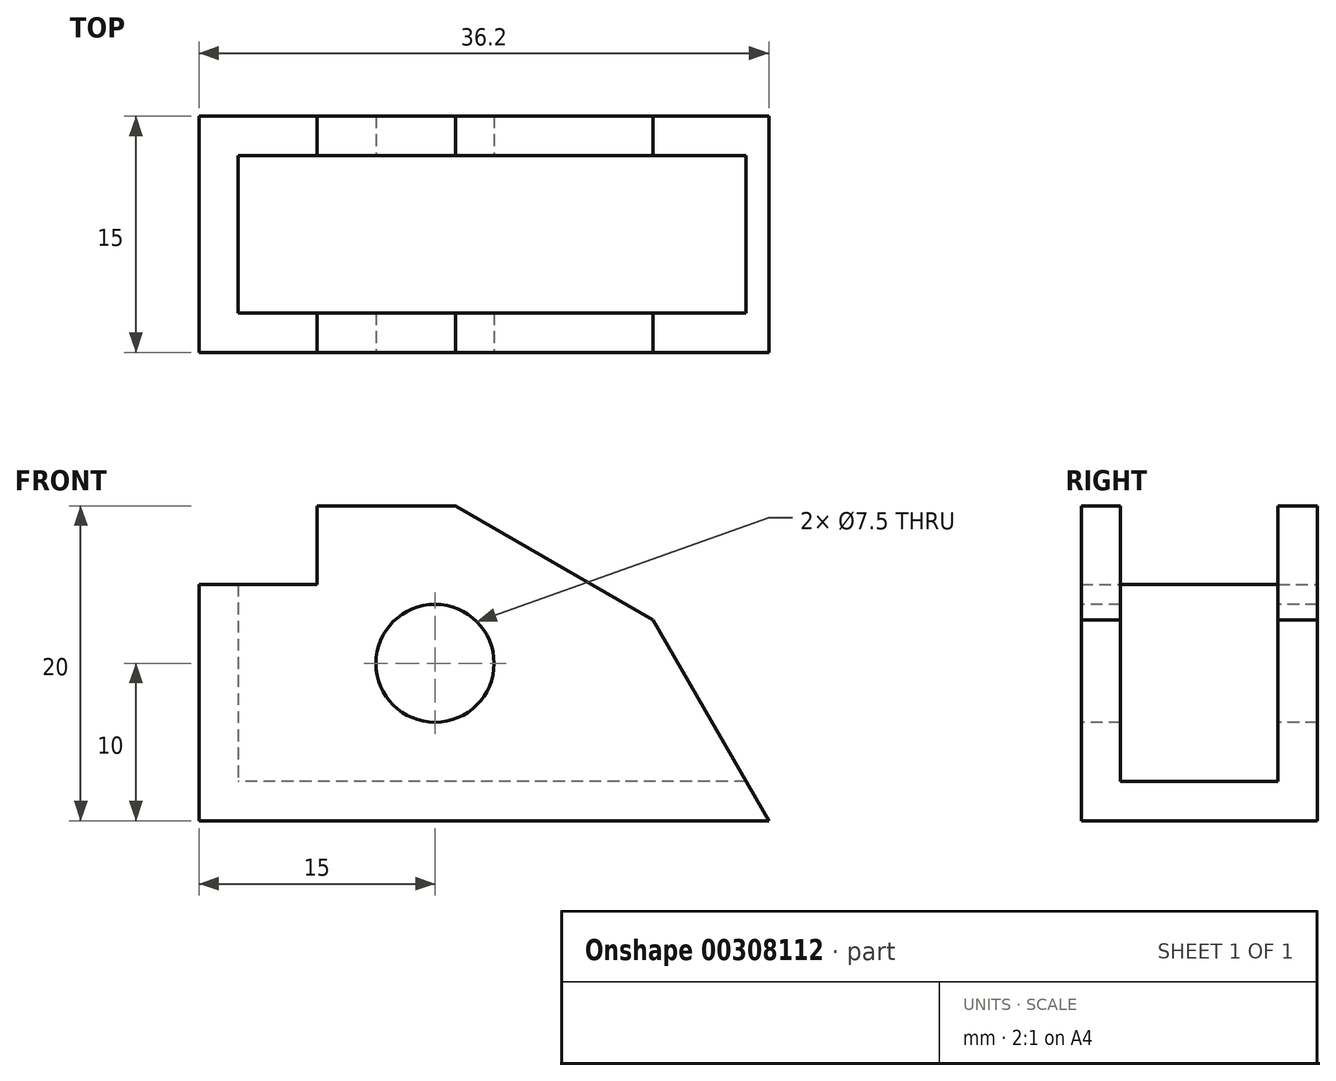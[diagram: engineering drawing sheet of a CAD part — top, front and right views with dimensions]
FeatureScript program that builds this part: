
annotation { "Feature Type Name" : "Feature", "Feature Type Description" : "" }
export const myFeature = defineFeature(function(context is Context, id is Id, definition is map)
    precondition{}
    {
        {
            var Q0;
            Q0=qCreatedBy(makeId("Front.planeOp"),FACE);
            var sketch = newSketch(context, id + "F0", { "sketchPlane" : qUnion([Q0])});
            skLineSegment(sketch, "E0", {"start": v(0, 0) * mm, "end": v(0, 15) * mm});
            skLineSegment(sketch, "E1", {"start": v(0, 15) * mm, "end": v(7.5, 15) * mm});
            skLineSegment(sketch, "E2", {"start": v(7.5, 15) * mm, "end": v(7.5, 20) * mm});
            skLineSegment(sketch, "E3", {"start": v(7.5, 20) * mm, "end": v(16.3, 20) * mm});
            skLineSegment(sketch, "E4", {"start": v(16.3, 20) * mm, "end": v(28.83, 12.77) * mm});
            skLineSegment(sketch, "E5", {"start": v(28.83, 12.77) * mm, "end": v(36.2, 0) * mm});
            skLineSegment(sketch, "E6", {"start": v(36.2, 0) * mm, "end": v(0, 0) * mm});
            skSolve(sketch);
        }
        {
            var Q0;
            Q0 = qSketchRegion(id + "F0", true);
            extrude(context, id + "F1", {"entities" : qUnion([Q0]), "depth" : 15 * mm});
        }
        {
            var Q0;
            Q0=makeQuery(id+"F1.opExtrude","SWEPT_FACE",FACE,{"disambiguationData":[OSD([sQuery(id+"F0.wireOp",EDGE,"E0")])]});
            var sketch = newSketch(context, id + "F2", { "sketchPlane" : qUnion([Q0])});
            skLineSegment(sketch, "E7", {"start": v(2.5, 22.5) * mm, "end": v(2.5, 2.5) * mm});
            skLineSegment(sketch, "E8", {"start": v(2.5, 2.5) * mm, "end": v(12.5, 2.5) * mm});
            skLineSegment(sketch, "E9", {"start": v(12.5, 2.5) * mm, "end": v(12.5, 22.5) * mm});
            skLineSegment(sketch, "E10", {"start": v(2.5, 22.5) * mm, "end": v(12.5, 22.5) * mm});
            skSolve(sketch);
        }
        {
            var Q0;
            {var subQ0=sQuery(id+"F2.wireOp",EDGE,"E10");Q0=makeQuery(id+"F2.imprint","IMPRINT",FACE,{"disambiguationData":[TD([[makeQuery(id+"F2.imprint","IMPRINT",EDGE,{"derivedFrom":subQ0}),-1.0]])]});}
            var Q1;
            {var subQ0=sQuery(id+"F2.wireOp",EDGE,"E8");Q1=makeQuery(id+"F2.imprint","IMPRINT",FACE,{"disambiguationData":[TD([[makeQuery(id+"F2.imprint","IMPRINT",EDGE,{"derivedFrom":subQ0}),1.0]])]});}
            extrude(context, id + "F3", {"entities" : qUnion([Q0, Q1]), "operationType" : NewBodyOperationType.REMOVE, "oppositeDirection" : true, "depth" : 40 * mm});
        }
        {
            var Q0;
            Q0=makeQuery(id+"F1.opExtrude","CAP_FACE",FACE,{"disambiguationData":[OSD([sQuery(id+"F0.wireOp",EDGE,"E0"),sQuery(id+"F0.wireOp",EDGE,"E1"),sQuery(id+"F0.wireOp",EDGE,"E2"),sQuery(id+"F0.wireOp",EDGE,"E3"),sQuery(id+"F0.wireOp",EDGE,"E4"),sQuery(id+"F0.wireOp",EDGE,"E5"),sQuery(id+"F0.wireOp",EDGE,"E6")])],"isStart":false});
            var sketch = newSketch(context, id + "F4", { "sketchPlane" : qUnion([Q0])});
            skCircle(sketch, "E11", {"center": v(15, 10) * mm, "radius": 3.75 * mm});
            skSolve(sketch);
        }
        {
            var Q0;
            Q0=makeQuery(id+"F4.imprint","IMPRINT",FACE,{"disambiguationData":[TD([[makeQuery(id+"F4.imprint","IMPRINT",EDGE,{"derivedFrom":sQuery(id+"F4.wireOp",EDGE,"E11")}),1.0]])]});
            extrude(context, id + "F5", {"entities" : qUnion([Q0]), "operationType" : NewBodyOperationType.REMOVE, "oppositeDirection" : true, "depth" : 29 * mm});
        }
        {
            var Q0;
            Q0=makeQuery(id+"F3.boolean.opBoolean","COPY",FACE,{"derivedFrom":makeQuery(id+"F3.opExtrude","SWEPT_FACE",FACE,{"disambiguationData":[OSD([sQuery(id+"F2.wireOp",EDGE,"E8")])]})});
            var sketch = newSketch(context, id + "F6", { "sketchPlane" : qUnion([Q0])});
            skLineSegment(sketch, "E12", {"start": v(0, -2.5) * mm, "end": v(2.5, -2.5) * mm});
            skLineSegment(sketch, "E13", {"start": v(2.5, -2.5) * mm, "end": v(2.5, -12.5) * mm});
            skLineSegment(sketch, "E14", {"start": v(2.5, -12.5) * mm, "end": v(0, -12.5) * mm});
            skLineSegment(sketch, "E15", {"start": v(0, -12.5) * mm, "end": v(0, -2.5) * mm});
            skSolve(sketch);
        }
        {
            var Q0;
            Q0=makeQuery(id+"F6.imprint","IMPRINT",FACE,{"disambiguationData":[TD([[makeQuery(id+"F6.imprint","IMPRINT",EDGE,{"derivedFrom":sQuery(id+"F6.wireOp",EDGE,"E12")}),1.0]])]});
            extrude(context, id + "F7", {"entities" : qUnion([Q0]), "operationType" : NewBodyOperationType.ADD, "depth" : 12.5 * mm});
        }
    });
